# Revit family: Утепленная заслонка AIRNED-M K1-2U
name_source: partatom
category: Оборудование
revit_build: Autodesk Revit 2017 (Build: 20160225_1515(x64)
units: mm (PartAtom-declared; Revit-internal decimal feet)

## family parameters
Всегда вертикально = Да
На основе рабочей плоскости = Нет
Общий = Нет
При загрузке вырезать с полостями = Нет
Размер круглого соединителя = Использовать диаметр
Тип детали = Нормальный
Точка расчета площади = Нет

## types (16) — shared parameters
Д = 172 мм
Единица измерения = шт.
Завод изготовитель = NED
Ключевая пометка = Вентиляция
Материал = Сталь серая
Раздел = ОВ

## per-type parameters (varying)
- AIRNED-M 6.K1U: d=15 мм; А=1000 мм; А1=1084 мм; А2=1026 мм; А3=1042 мм; Б2=440 мм; В1=564 мм; В2=526 мм; В3=542 мм; Высота=4015 мм; Мощность, кВт=2 Вт; Наименование и тех.хар-ка=Торцевая утепленная заслонка; Напряжение U,В=1-220/3-380; Середина=282 мм; Тип, марка, обозначение=AIRNED-M 6.K1U; Ширина=1550 мм; Ширина лопатки=113 мм; пл=50 мм; р=129 мм; размер В=500 мм; №12=Нет; №20=Нет; №25=Нет; №30=Нет; №35=Нет; №6=Да; №7=Нет; №8=Нет
- AIRNED-M 7.K1U: d=15 мм; А=1000 мм; А1=1084 мм; А2=1026 мм; А3=1042 мм; Б2=640 мм; В1=764 мм; В2=726 мм; В3=742 мм; Высота=1245 мм; Мощность, кВт=3 Вт; Наименование и тех.хар-ка=Торцевая утепленная заслонка; Напряжение U,В=1-220/3-380; Середина=382 мм; Тип, марка, обозначение=AIRNED-M 7.K1U; Ширина=1025 мм; Ширина лопатки=158 мм; пл=70 мм; р=181 мм; размер В=700 мм; №12=Нет; №20=Нет; №25=Нет; №30=Нет; №35=Нет; №6=Нет; №7=Да; №8=Нет
- AIRNED-M 8.K1U: d=18 мм; А=1200 мм; А1=1284 мм; А2=1226 мм; А3=1242 мм; Б2=640 мм; В1=764 мм; В2=726 мм; В3=742 мм; Высота=1245 мм; Мощность, кВт=3 Вт; Наименование и тех.хар-ка=Торцевая утепленная заслонка; Напряжение U,В=1-220/3-380; Середина=382 мм; Тип, марка, обозначение=AIRNED-M 8.K1U; Ширина=1550 мм; Ширина лопатки=158 мм; пл=70 мм; р=181 мм; размер В=700 мм; №12=Нет; №20=Нет; №25=Нет; №30=Нет; №35=Нет; №6=Нет; №7=Нет; №8=Да
- AIRNED-M 12.K1U: d=20 мм; А=1330 мм; А1=1414 мм; А2=1356 мм; А3=1372 мм; Б2=740 мм; В1=864 мм; В2=826 мм; В3=842 мм; Высота=1360 мм; Мощность, кВт=4 Вт; Наименование и тех.хар-ка=Торцевая утепленная заслонка; Напряжение U,В=1-220/3-380; Середина=432 мм; Тип, марка, обозначение=AIRNED-M 12.K1U; Ширина=1550 мм; Ширина лопатки=180 мм; пл=80 мм; р=206 мм; размер В=800 мм; №12=Да; №20=Нет; №25=Нет; №30=Нет; №35=Нет; №6=Нет; №7=Нет; №8=Нет
- AIRNED-M 20.K1U: d=24 мм; А=1550 мм; А1=1634 мм; А2=1576 мм; А3=1592 мм; Б2=940 мм; В1=1064 мм; В2=1026 мм; В3=1042 мм; Высота=1585 мм; Мощность, кВт=6 Вт; Наименование и тех.хар-ка=Торцевая утепленная заслонка; Напряжение U,В=3-380; Середина=532 мм; Тип, марка, обозначение=AIRNED-M 20.K1U; Ширина=1550 мм; Ширина лопатки=225 мм; пл=100 мм; р=258 мм; размер В=1000 мм; №12=Нет; №20=Да; №25=Нет; №30=Нет; №35=Нет; №6=Нет; №7=Нет; №8=Нет
- AIRNED-M 25.K1U: d=29 мм; А=1860 мм; А1=1944 мм; А2=1886 мм; А3=1902 мм; Б2=1340 мм; В1=1464 мм; В2=1426 мм; В3=1442 мм; Высота=1970 мм; Мощность, кВт=9 Вт; Наименование и тех.хар-ка=Торцевая утепленная заслонка; Напряжение U,В=1-220/3-380; Середина=732 мм; Тип, марка, обозначение=AIRNED-M 25.K1U; Ширина=1550 мм; Ширина лопатки=315 мм; пл=140 мм; р=361 мм; размер В=1400 мм; №12=Нет; №20=Нет; №25=Да; №30=Нет; №35=Нет; №6=Нет; №7=Нет; №8=Нет
- AIRNED-M 30.K1U: d=35 мм; А=2300 мм; А1=2384 мм; А2=2326 мм; А3=2342 мм; Б2=1340 мм; В1=1464 мм; В2=1426 мм; В3=1442 мм; Высота=1970 мм; Мощность, кВт=12 Вт; Наименование и тех.хар-ка=Торцевая утепленная заслонка; Напряжение U,В=3-380; Середина=732 мм; Тип, марка, обозначение=AIRNED-M 30.K1U; Ширина=2075 мм; Ширина лопатки=315 мм; пл=140 мм; р=361 мм; размер В=1400 мм; №12=Нет; №20=Нет; №25=Нет; №30=Да; №35=Нет; №6=Нет; №7=Нет; №8=Нет
- AIRNED-M 35.K1U: d=35 мм; А=2300 мм; А1=2384 мм; А2=2326 мм; А3=2342 мм; Б2=1840 мм; В1=1964 мм; В2=1926 мм; В3=1942 мм; Высота=2410 мм; Мощность, кВт=16 Вт; Наименование и тех.хар-ка=Торцевая утепленная заслонка; Напряжение U,В=3-380; Середина=982 мм; Тип, марка, обозначение=AIRNED-M 35.K1U; Ширина=2075 мм; Ширина лопатки=428 мм; пл=190 мм; р=490 мм; размер В=1900 мм; №12=Нет; №20=Нет; №25=Нет; №30=Нет; №35=Да; №6=Нет; №7=Нет; №8=Нет
- AIRNED-M 6.K2U: d=15 мм; А=1000 мм; А1=1084 мм; А2=1026 мм; А3=1042 мм; Б2=440 мм; В1=564 мм; В2=526 мм; В3=542 мм; Высота=4015 мм; Мощность, кВт=2 Вт; Наименование и тех.хар-ка=Верхняя утепленная заслонка; Напряжение U,В=1-220/3-380; Середина=282 мм; Тип, марка, обозначение=AIRNED-M 6.K2U; Ширина=1550 мм; Ширина лопатки=113 мм; пл=50 мм; р=129 мм; размер В=500 мм; №12=Нет; №20=Нет; №25=Нет; №30=Нет; №35=Нет; №6=Да; №7=Нет; №8=Нет
- AIRNED-M 7.K2U: d=15 мм; А=1000 мм; А1=1084 мм; А2=1026 мм; А3=1042 мм; Б2=640 мм; В1=764 мм; В2=726 мм; В3=742 мм; Высота=1245 мм; Мощность, кВт=2 Вт; Наименование и тех.хар-ка=Верхняя утепленная заслонка; Напряжение U,В=1-220/3-380; Середина=382 мм; Тип, марка, обозначение=AIRNED-M 7.K1U; Ширина=1025 мм; Ширина лопатки=158 мм; пл=70 мм; р=181 мм; размер В=700 мм; №12=Нет; №20=Нет; №25=Нет; №30=Нет; №35=Нет; №6=Нет; №7=Да; №8=Нет
- AIRNED-M 8.K2U: d=18 мм; А=1200 мм; А1=1284 мм; А2=1226 мм; А3=1242 мм; Б2=440 мм; В1=564 мм; В2=526 мм; В3=542 мм; Высота=1245 мм; Мощность, кВт=2 Вт; Наименование и тех.хар-ка=Верхняя утепленная заслонка; Напряжение U,В=1-220/3-380; Середина=282 мм; Тип, марка, обозначение=AIRNED-M 8.K2U; Ширина=1550 мм; Ширина лопатки=113 мм; пл=50 мм; р=129 мм; размер В=500 мм; №12=Нет; №20=Нет; №25=Нет; №30=Нет; №35=Нет; №6=Нет; №7=Нет; №8=Да
- AIRNED-M 12.K2U: d=20 мм; А=1330 мм; А1=1414 мм; А2=1356 мм; А3=1372 мм; Б2=940 мм; В1=1064 мм; В2=1026 мм; В3=1042 мм; Высота=1360 мм; Мощность, кВт=5 Вт; Наименование и тех.хар-ка=Верхняя утепленная заслонка; Напряжение U,В=1-220/3-380; Середина=532 мм; Тип, марка, обозначение=AIRNED-M 12.K2U; Ширина=1550 мм; Ширина лопатки=225 мм; пл=100 мм; р=258 мм; размер В=1000 мм; №12=Да; №20=Нет; №25=Нет; №30=Нет; №35=Нет; №6=Нет; №7=Нет; №8=Нет
- AIRNED-M 20.K2U: d=24 мм; А=1550 мм; А1=1634 мм; А2=1576 мм; А3=1592 мм; Б2=940 мм; В1=1064 мм; В2=1026 мм; В3=1042 мм; Высота=1585 мм; Мощность, кВт=6 Вт; Наименование и тех.хар-ка=Верхняя утепленная заслонка; Напряжение U,В=3-380; Середина=532 мм; Тип, марка, обозначение=AIRNED-M 20.K2U; Ширина=1550 мм; Ширина лопатки=225 мм; пл=100 мм; р=258 мм; размер В=1000 мм; №12=Нет; №20=Да; №25=Нет; №30=Нет; №35=Нет; №6=Нет; №7=Нет; №8=Нет
- AIRNED-M 25.K2U: d=29 мм; А=1860 мм; А1=1944 мм; А2=1886 мм; А3=1902 мм; Б2=940 мм; В1=1064 мм; В2=1026 мм; В3=1042 мм; Высота=1970 мм; Мощность, кВт=8 Вт; Наименование и тех.хар-ка=Верхняя утепленная заслонка; Напряжение U,В=1-220/3-380; Середина=532 мм; Тип, марка, обозначение=AIRNED-M 25.K2U; Ширина=1550 мм; Ширина лопатки=225 мм; пл=100 мм; р=258 мм; размер В=1000 мм; №12=Нет; №20=Нет; №25=Да; №30=Нет; №35=Нет; №6=Нет; №7=Нет; №8=Нет
- AIRNED-M 30.K2U: d=35 мм; А=2300 мм; А1=2384 мм; А2=2326 мм; А3=2342 мм; Б2=940 мм; В1=1064 мм; В2=1026 мм; В3=1042 мм; Высота=1970 мм; Мощность, кВт=9 Вт; Наименование и тех.хар-ка=Верхняя утепленная заслонка; Напряжение U,В=1-220/3-380; Середина=532 мм; Тип, марка, обозначение=AIRNED-M 30.K2U; Ширина=2075 мм; Ширина лопатки=225 мм; пл=100 мм; р=258 мм; размер В=1000 мм; №12=Нет; №20=Нет; №25=Нет; №30=Да; №35=Нет; №6=Нет; №7=Нет; №8=Нет
- AIRNED-M 35.K2U: d=35 мм; А=2300 мм; А1=2384 мм; А2=2326 мм; А3=2342 мм; Б2=1440 мм; В1=1564 мм; В2=1526 мм; В3=1542 мм; Высота=2410 мм; Мощность, кВт=13 Вт; Наименование и тех.хар-ка=Верхняя утепленная заслонка; Напряжение U,В=3-380; Середина=782 мм; Тип, марка, обозначение=AIRNED-M 35.K2U; Ширина=2075 мм; Ширина лопатки=338 мм; пл=150 мм; р=387 мм; размер В=1500 мм; №12=Нет; №20=Нет; №25=Нет; №30=Нет; №35=Да; №6=Нет; №7=Нет; №8=Нет
